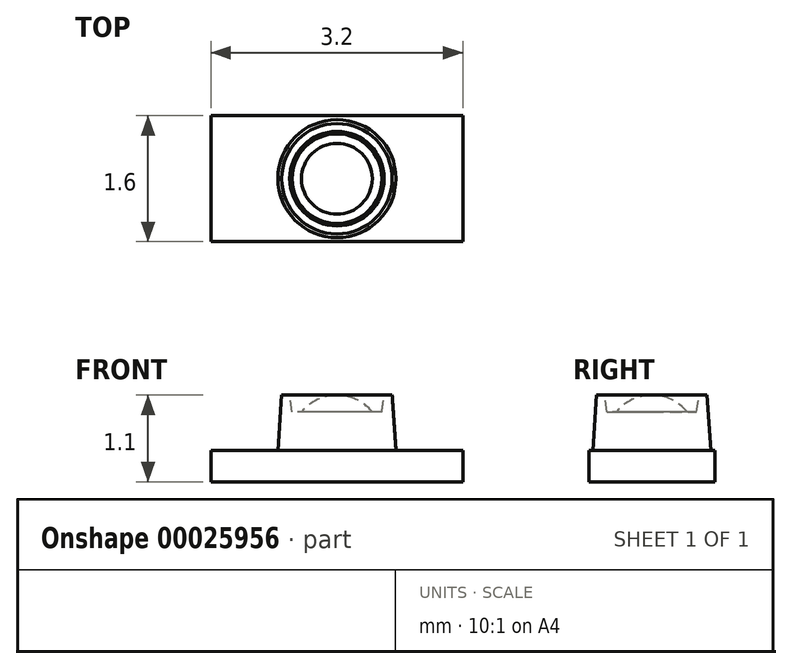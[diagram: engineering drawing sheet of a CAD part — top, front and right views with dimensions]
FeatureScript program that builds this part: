
annotation { "Feature Type Name" : "Feature", "Feature Type Description" : "" }
export const myFeature = defineFeature(function(context is Context, id is Id, definition is map)
    precondition{}
    {
        {
            var Q0;
            Q0=qCreatedBy(makeId("Top.planeOp"),FACE);
            var sketch = newSketch(context, id + "F0", { "sketchPlane" : qUnion([Q0])});
            skLineSegment(sketch, "E0.rect.bottom", {"start": v(1.6, -0.8) * mm, "end": v(-1.6, -0.8) * mm});
            skLineSegment(sketch, "E0.rect.top", {"start": v(1.6, 0.8) * mm, "end": v(-1.6, 0.8) * mm});
            skLineSegment(sketch, "E0.rect.left", {"start": v(1.6, -0.8) * mm, "end": v(1.6, 0.8) * mm});
            skLineSegment(sketch, "E0.rect.right", {"start": v(-1.6, -0.8) * mm, "end": v(-1.6, 0.8) * mm});
            skPoint(sketch, "E0.rect.middle", {"position": v(0, 0) * mm});
            skSolve(sketch);
        }
        {
            var Q0;
            Q0 = qSketchRegion(id + "F0", true);
            extrude(context, id + "F1", {"entities" : qUnion([Q0]), "depth" : .4 * mm});
        }
        {
            var Q0;
            Q0=makeQuery(id+"F1.opExtrude","CAP_FACE",FACE,{"disambiguationData":[OSD([sQuery(id+"F0.wireOp",EDGE,"E0.rect.bottom"),sQuery(id+"F0.wireOp",EDGE,"E0.rect.top"),sQuery(id+"F0.wireOp",EDGE,"E0.rect.left"),sQuery(id+"F0.wireOp",EDGE,"E0.rect.right")])],"isStart":false});
            var sketch = newSketch(context, id + "F2", { "sketchPlane" : qUnion([Q0])});
            skCircle(sketch, "E1", {"center": v(0, 0) * mm, "radius": 0.75 * mm});
            skSolve(sketch);
        }
        {
            var Q0;
            Q0 = qSketchRegion(id + "F2", true);
            extrude(context, id + "F3", {"entities" : qUnion([Q0]), "operationType" : NewBodyOperationType.ADD, "depth" : .7 * mm, "hasDraft" : true, "draftAngle" : 4 * degree, "draftPullDirection" : true});
        }
        {
            var Q0;
            Q0=qCreatedBy(makeId("Front.planeOp"),FACE);
            var sketch = newSketch(context, id + "F4", { "sketchPlane" : qUnion([Q0])});
            skLineSegment(sketch, "E2", {"start": v(0, 0) * mm, "end": v(0, 1.88) * mm, "construction": true});
            skLineSegment(sketch, "E3", {"start": v(0.6, 1.1) * mm, "end": v(0.57, 0.89) * mm});
            skLineSegment(sketch, "E4", {"start": v(0.57, 0.89) * mm, "end": v(0.45, 0.89) * mm});
            skArc(sketch, "E5", {"start": v(0.45, 0.89) * mm, "mid": v(0.25, 1.04) * mm, "end": v(0, 1.1) * mm});
            skLineSegment(sketch, "E6", {"start": v(0, 1.1) * mm, "end": v(0, 1.26) * mm});
            skLineSegment(sketch, "E7", {"start": v(0.6, 1.1) * mm, "end": v(0.6, 1.26) * mm});
            skLineSegment(sketch, "E8", {"start": v(0.6, 1.26) * mm, "end": v(0, 1.26) * mm});
            skSolve(sketch);
        }
        {
            var Q0;
            Q0 = qSketchRegion(id + "F4", true);
            var Q1;
            Q1=sQuery(id+"F4.wireOp",EDGE,"E2");
            revolve(context, id + "F5", {"operationType" : NewBodyOperationType.REMOVE, "entities" : qUnion([Q0]), "axis" : qUnion([Q1]), "revolveType" : RevolveType.FULL, "oppositeDirection" : true});
        }
    });
